# Revit family: BDG_BossDesign_Stng_ATOM_IndividualEndUnit
name_source: partatom
category: Furniture
revit_build: Autodesk Revit 2015 (Build: 20140903_1530(x64)
units: mm (PartAtom-declared; Revit-internal decimal feet)

## types (6) — shared parameters
Assembly Code = E2020200
AssetType = Movable
BIMObjectName = BDG_BossDesign_Seating_ATOM_IndividualEndUnit
Category = Pr_40_50_12 : Chairs, seats and benches
Color = Various
DurationUnit = year
ExpectedLife = 5
Finish = Fabric
IfcExportAs = IfcFurnishingElementType
IfcExportType = SOFA
Keynote = Pr_40_50_12
MainColor = Various
ManufacturerName = Boss Design
ManufacturerURL = www.bossdesign.com
Material = Upholstered
NBSDescription = Seating
NBSReference = 45-35-72/352
Name = Seating_ATOM_IndividualEndUnit_BossDesign
NominalLength = 1100 mm
Shape = Rectangular
URL = www.bossdesign.com
Uniclass2015Code = Pr_40_50_12
Uniclass2015Title = Chairs, seats and benches
Uniclass2015Version = Products v1.9
Version = 1
WarrantyDescription = Structural Warranty Excludes Foams and Fabrics
WarrantyDurationLabor = 5
WarrantyDurationParts = 5
WarrantyDurationUnit = year

## per-type parameters (varying)
| type | Description | IsATOLHAH | IsATOLHAL | IsATOLHB | IsATORHAH | IsATORHAL | IsATORHB | IsLeft | IsLeftArm | IsRight | IsRightArm | ModelReference | NominalHeight | NominalWidth | Size |
| ATO/RHA/L | ATOM Right Hand Arm Low Back Seating Unit | No | No | No | No | Yes | No | No | No | Yes | Yes | ATOM Right Hand Arm Low Back Seating Unit | 1010 mm | 850 mm | 1100 x 850 x 1010mm |
| ATO/LHA/L | ATOM Left Hand Arm Low Back Seating Unit | No | Yes | No | No | No | No | Yes | Yes | No | No | ATOM Left Hand Arm Low Back Seating Unit | 1010 mm | 850 mm | 1100 x 850 x 1010mm |
| ATO/RHB | ATOM Right Hand Booth Arm Seating Unit | No | No | No | No | No | Yes | No | No | Yes | No | ATOM Right Hand Booth Arm Seating Unit | 1390 mm | 950 mm | 1100 x 950 x 1390mm |
| ATO/LHB | ATOM Left Hand Booth Arm Seating Unit | No | No | Yes | No | No | No | Yes | Yes | No | No | ATOM Left Hand Booth Arm Seating Unit | 1390 mm | 950 mm | 1100 x 950 x 1390mm |
| ATO/RHA/H | ATOM Right Hand Arm High Back Seating Unit | No | No | No | Yes | No | No | No | No | Yes | Yes | ATOM Right Hand Arm High Back Seating Unit | 1390 mm | 850 mm | 1100 x 850 x 1390mm |
| ATO/LHA/H | ATOM Left Hand Arm High Back Seating Unit | Yes | No | No | No | No | No | Yes | Yes | No | No | ATOM Left Hand Arm High Back Seating Unit | 1390 mm | 850 mm | 1100 x 850 x 1390mm |

note: column(s) folded — value = type name in every type: Model, ModelNumber

## geometry (parser evidence)
native form markers: Sweep x2
no freeform markers — native parametric forms only
